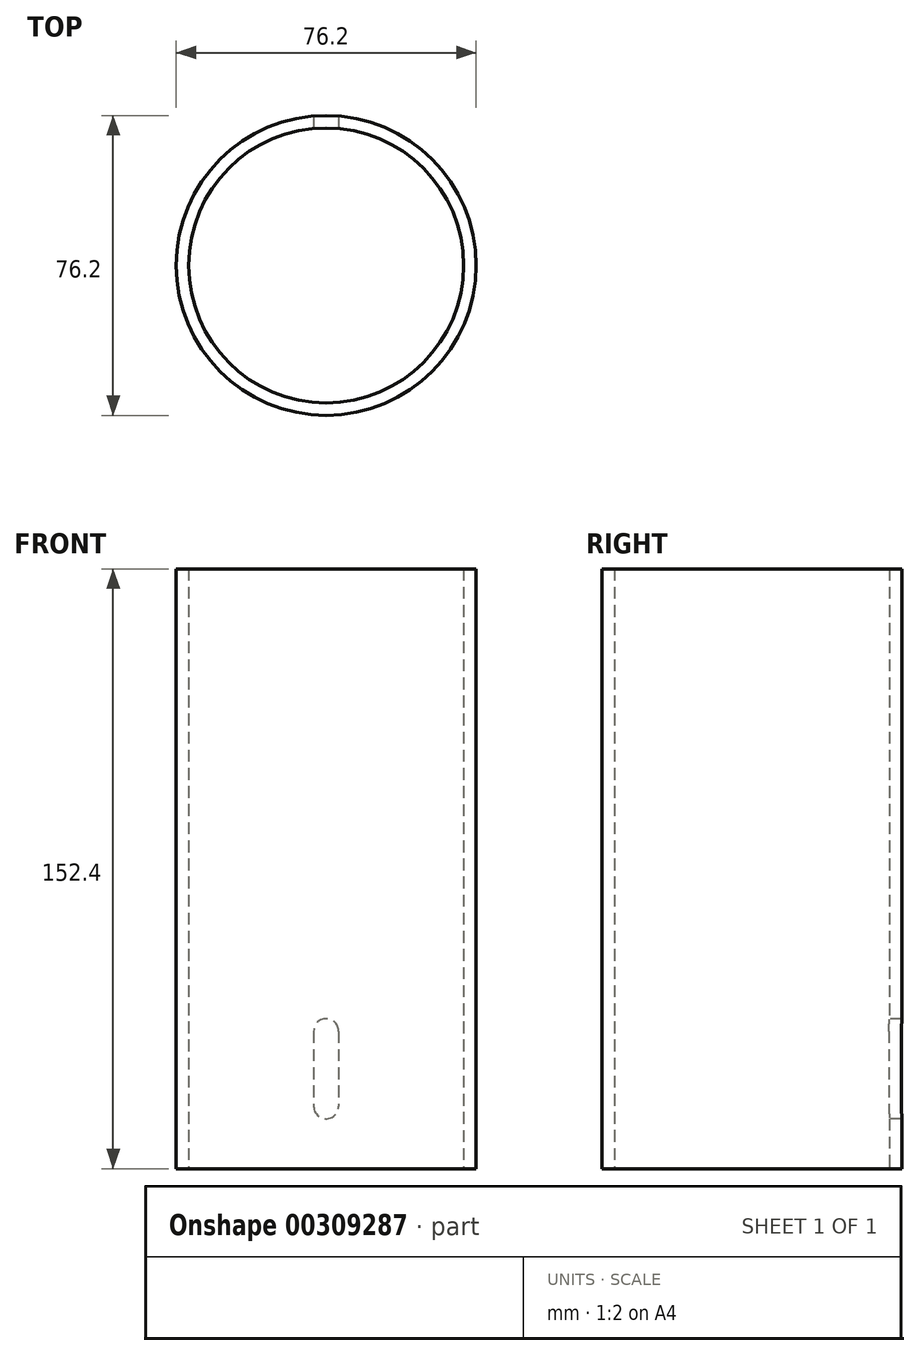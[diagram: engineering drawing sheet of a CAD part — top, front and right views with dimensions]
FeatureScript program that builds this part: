
annotation { "Feature Type Name" : "Feature", "Feature Type Description" : "" }
export const myFeature = defineFeature(function(context is Context, id is Id, definition is map)
    precondition{}
    {
        {
            var Q0;
            Q0=qCreatedBy(makeId("Top.planeOp"),FACE);
            var sketch = newSketch(context, id + "F0", { "sketchPlane" : qUnion([Q0])});
            skCircle(sketch, "E0", {"center": v(0, 0) * mm, "radius": 38.1 * mm});
            skCircle(sketch, "E1", {"center": v(0, 0) * mm, "radius": 34.93 * mm});
            skSolve(sketch);
        }
        {
            var Q0;
            Q0=qSketchRegion(id+"F0",true);
            extrude(context, id + "F1", {"entities" : qUnion([Q0]), "depth" : 152.4 * mm});
        }
        {
            var Q0;
            Q0=qCreatedBy(makeId("Front.planeOp"),FACE);
            var sketch = newSketch(context, id + "F2", { "sketchPlane" : qUnion([Q0])});
            skLineSegment(sketch, "E2.left", {"start": v(3.17, 15.87) * mm, "end": v(3.17, 34.93) * mm});
            skLineSegment(sketch, "E2.right", {"start": v(-3.18, 15.87) * mm, "end": v(-3.18, 34.93) * mm});
            skPoint(sketch, "E2.middle", {"position": v(0, 25.4) * mm});
            skArc(sketch, "E3", {"start": v(3.17, 34.93) * mm, "mid": v(0, 38.1) * mm, "end": v(-3.17, 34.93) * mm});
            skArc(sketch, "E4", {"start": v(-3.17, 15.87) * mm, "mid": v(0, 12.7) * mm, "end": v(3.17, 15.87) * mm});
            skLineSegment(sketch, "E5", {"start": v(0, 34.93) * mm, "end": v(0, 15.87) * mm});
            skSolve(sketch);
        }
        {
            var Q0;
            Q0=makeQuery(id+"F2.imprint","IMPRINT",FACE,{"disambiguationData":[TD([[makeQuery(id+"F2.imprint","IMPRINT",EDGE,{"derivedFrom":sQuery(id+"F2.wireOp",EDGE,"E2.left")}),1.0]])]});
            extrude(context, id + "F3", {"entities" : qUnion([Q0]), "operationType" : NewBodyOperationType.REMOVE, "endBound" : BoundingType.THROUGH_ALL, "oppositeDirection" : true, "depth" : 25.4 * mm});
        }
    });
